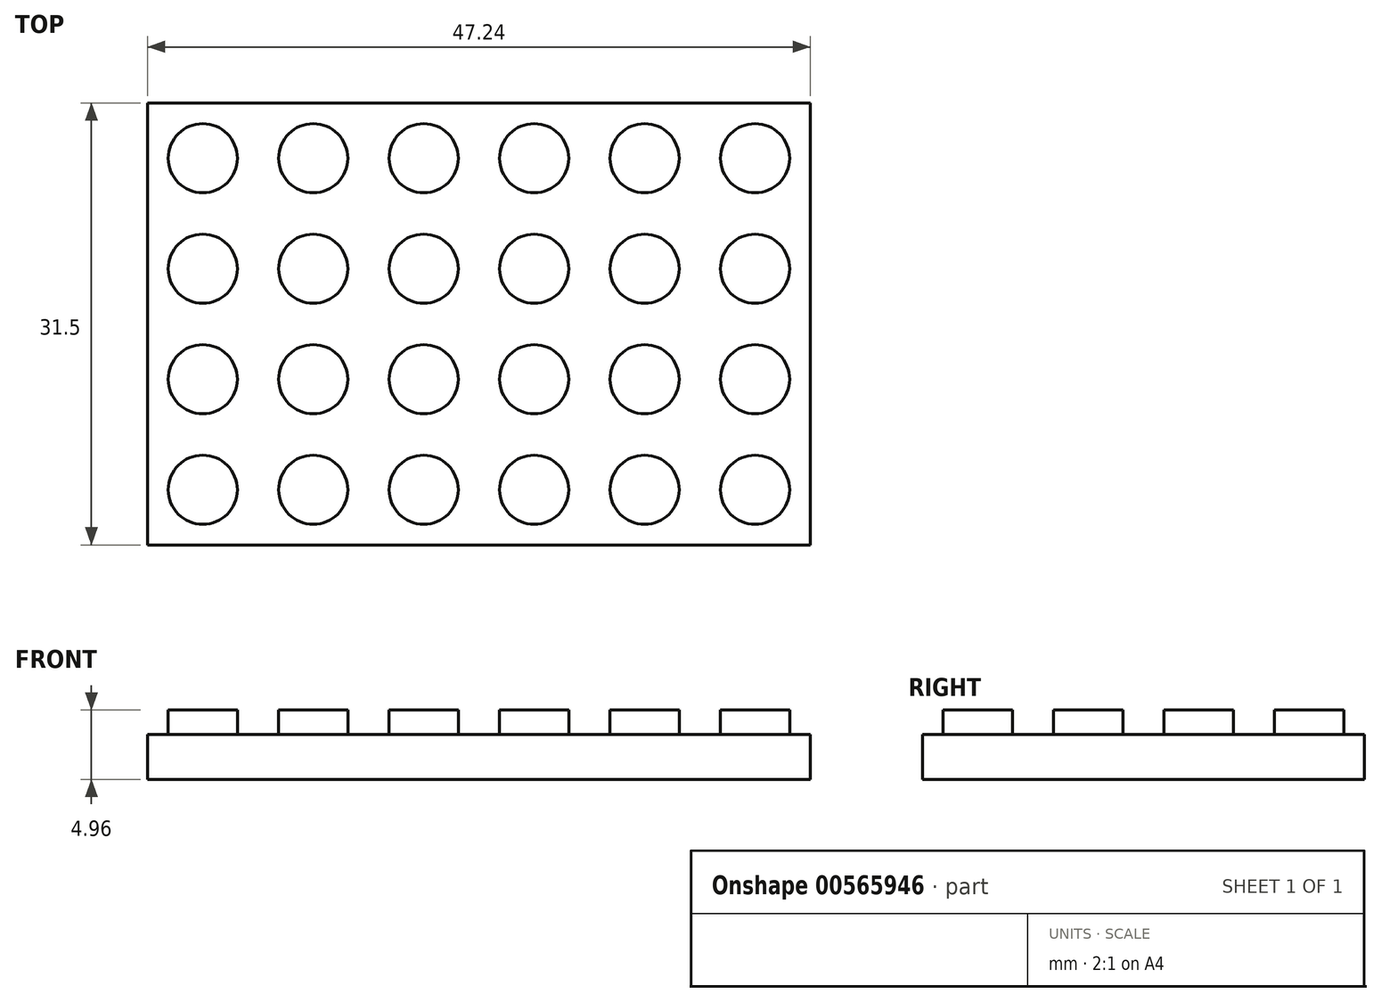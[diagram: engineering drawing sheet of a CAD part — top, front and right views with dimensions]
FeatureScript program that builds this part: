
annotation { "Feature Type Name" : "Feature", "Feature Type Description" : "" }
export const myFeature = defineFeature(function(context is Context, id is Id, definition is map)
    precondition{}
    {
        {
            var Q0;
            Q0=qCreatedBy(makeId("Top.planeOp"),FACE);
            var sketch = newSketch(context, id + "F0", { "sketchPlane" : qUnion([Q0])});
            skLineSegment(sketch, "E0.rect.bottom", {"start": v(23.62, 15.75) * mm, "end": v(-23.62, 15.75) * mm});
            skLineSegment(sketch, "E0.rect.top", {"start": v(23.62, -15.75) * mm, "end": v(-23.62, -15.75) * mm});
            skLineSegment(sketch, "E0.rect.left", {"start": v(23.62, 15.75) * mm, "end": v(23.62, -15.75) * mm});
            skLineSegment(sketch, "E0.rect.right", {"start": v(-23.62, 15.75) * mm, "end": v(-23.62, -15.75) * mm});
            skPoint(sketch, "E0.rect.middle", {"position": v(0, 0) * mm});
            skSolve(sketch);
        }
        {
            var Q0;
            Q0=makeQuery(id+"F0.imprint","IMPRINT",FACE,{"disambiguationData":[TD([[makeQuery(id+"F0.imprint","IMPRINT",EDGE,{"derivedFrom":sQuery(id+"F0.wireOp",EDGE,"E0.rect.bottom")}),1.0]])]});
            extrude(context, id + "F1", {"entities" : qUnion([Q0]), "depth" : 3.2 * mm});
        }
        {
            var Q0;
            Q0=makeQuery(id+"F1.opExtrude","CAP_FACE",FACE,{"disambiguationData":[OSD([sQuery(id+"F0.wireOp",EDGE,"E0.rect.bottom"),sQuery(id+"F0.wireOp",EDGE,"E0.rect.top"),sQuery(id+"F0.wireOp",EDGE,"E0.rect.left"),sQuery(id+"F0.wireOp",EDGE,"E0.rect.right")])],"isStart":false});
            var sketch = newSketch(context, id + "F2", { "sketchPlane" : qUnion([Q0])});
            skLineSegment(sketch, "E1", {"start": v(0, 0) * mm, "end": v(0, 7.87) * mm});
            skLineSegment(sketch, "E2", {"start": v(0, 7.87) * mm, "end": v(0, 15.75) * mm});
            skLineSegment(sketch, "E3", {"start": v(0, 0) * mm, "end": v(0, -7.87) * mm});
            skLineSegment(sketch, "E4", {"start": v(0, -7.87) * mm, "end": v(0, -15.75) * mm});
            skPoint(sketch, "E4.endSnap0", {"position": v(0, -15.75) * mm});
            skLineSegment(sketch, "E5", {"start": v(0, 0) * mm, "end": v(3.94, 0) * mm});
            skLineSegment(sketch, "E6", {"start": v(3.94, 0) * mm, "end": v(11.81, 0) * mm});
            skLineSegment(sketch, "E7", {"start": v(11.81, 0) * mm, "end": v(19.69, 0) * mm});
            skLineSegment(sketch, "E8", {"start": v(0, 0) * mm, "end": v(-3.94, 0) * mm});
            skLineSegment(sketch, "E9", {"start": v(-3.94, 0) * mm, "end": v(-11.81, 0) * mm});
            skLineSegment(sketch, "E10", {"start": v(-11.81, 0) * mm, "end": v(-19.69, 0) * mm});
            skLineSegment(sketch, "E11", {"start": v(-19.69, 0) * mm, "end": v(-19.69, -3.94) * mm});
            skLineSegment(sketch, "E12", {"start": v(-19.69, -3.94) * mm, "end": v(-19.69, -11.81) * mm});
            skLineSegment(sketch, "E13", {"start": v(-19.69, 0) * mm, "end": v(-19.69, 3.94) * mm});
            skLineSegment(sketch, "E14", {"start": v(-19.69, 3.94) * mm, "end": v(-19.69, 11.81) * mm});
            skLineSegment(sketch, "E15", {"start": v(-19.69, 3.94) * mm, "end": v(-11.81, 3.94) * mm});
            skLineSegment(sketch, "E16", {"start": v(-11.81, 3.94) * mm, "end": v(-3.94, 3.94) * mm});
            skLineSegment(sketch, "E17", {"start": v(-3.94, 3.94) * mm, "end": v(-3.94, 11.81) * mm});
            skLineSegment(sketch, "E18", {"start": v(-3.94, 11.81) * mm, "end": v(-11.81, 11.81) * mm});
            skLineSegment(sketch, "E19", {"start": v(-19.69, -3.94) * mm, "end": v(-11.81, -3.94) * mm});
            skLineSegment(sketch, "E20", {"start": v(-11.81, -3.94) * mm, "end": v(-3.94, -3.94) * mm});
            skLineSegment(sketch, "E21", {"start": v(-3.94, -3.94) * mm, "end": v(-3.94, -11.81) * mm});
            skLineSegment(sketch, "E22", {"start": v(-3.94, -11.81) * mm, "end": v(-11.81, -11.81) * mm});
            skLineSegment(sketch, "E23", {"start": v(3.94, 0) * mm, "end": v(3.94, 3.94) * mm});
            skPoint(sketch, "E23.endSnap0", {"position": v(0, 3.94) * mm});
            skLineSegment(sketch, "E24", {"start": v(3.94, 3.94) * mm, "end": v(3.94, 11.81) * mm});
            skPoint(sketch, "E24.endSnap0", {"position": v(0, 11.81) * mm});
            skLineSegment(sketch, "E25", {"start": v(3.94, 11.81) * mm, "end": v(11.81, 11.81) * mm});
            skLineSegment(sketch, "E26", {"start": v(11.81, 11.81) * mm, "end": v(19.69, 11.81) * mm});
            skLineSegment(sketch, "E27", {"start": v(19.69, 11.81) * mm, "end": v(19.69, 3.94) * mm});
            skLineSegment(sketch, "E28", {"start": v(19.69, 3.94) * mm, "end": v(11.81, 3.94) * mm});
            skLineSegment(sketch, "E29", {"start": v(3.94, 0) * mm, "end": v(3.94, -3.94) * mm});
            skPoint(sketch, "E29.endSnap0", {"position": v(0, -3.94) * mm});
            skLineSegment(sketch, "E30", {"start": v(3.94, -3.94) * mm, "end": v(3.94, -11.81) * mm});
            skPoint(sketch, "E30.endSnap0", {"position": v(0, -11.81) * mm});
            skLineSegment(sketch, "E31", {"start": v(3.94, -11.81) * mm, "end": v(11.81, -11.81) * mm});
            skLineSegment(sketch, "E32", {"start": v(11.81, -11.81) * mm, "end": v(19.69, -11.81) * mm});
            skLineSegment(sketch, "E33", {"start": v(19.69, -11.81) * mm, "end": v(19.69, -3.94) * mm});
            skLineSegment(sketch, "E34", {"start": v(19.69, -3.94) * mm, "end": v(11.81, -3.94) * mm});
            skCircle(sketch, "E35", {"center": v(-19.69, 11.81) * mm, "radius": 2.46 * mm});
            skCircle(sketch, "E36", {"center": v(-11.81, 11.81) * mm, "radius": 2.46 * mm});
            skCircle(sketch, "E37", {"center": v(-3.94, 11.81) * mm, "radius": 2.46 * mm});
            skCircle(sketch, "E38", {"center": v(3.94, 11.81) * mm, "radius": 2.46 * mm});
            skCircle(sketch, "E39", {"center": v(11.81, 11.81) * mm, "radius": 2.46 * mm});
            skCircle(sketch, "E40", {"center": v(19.69, 11.81) * mm, "radius": 2.46 * mm});
            skCircle(sketch, "E41", {"center": v(19.69, 3.94) * mm, "radius": 2.46 * mm});
            skCircle(sketch, "E42", {"center": v(11.81, 3.94) * mm, "radius": 2.46 * mm});
            skCircle(sketch, "E43", {"center": v(3.94, 3.94) * mm, "radius": 2.46 * mm});
            skCircle(sketch, "E44", {"center": v(-3.94, 3.94) * mm, "radius": 2.46 * mm});
            skCircle(sketch, "E45", {"center": v(-11.81, 3.94) * mm, "radius": 2.46 * mm});
            skCircle(sketch, "E46", {"center": v(-19.69, 3.94) * mm, "radius": 2.46 * mm});
            skCircle(sketch, "E47", {"center": v(-19.69, -3.94) * mm, "radius": 2.46 * mm});
            skCircle(sketch, "E48", {"center": v(-11.81, -3.94) * mm, "radius": 2.46 * mm});
            skCircle(sketch, "E49", {"center": v(-3.94, -3.94) * mm, "radius": 2.46 * mm});
            skCircle(sketch, "E50", {"center": v(-3.94, -11.81) * mm, "radius": 2.46 * mm});
            skCircle(sketch, "E51", {"center": v(-11.81, -11.81) * mm, "radius": 2.46 * mm});
            skCircle(sketch, "E52", {"center": v(-19.69, -11.81) * mm, "radius": 2.46 * mm});
            skCircle(sketch, "E53", {"center": v(3.94, -11.81) * mm, "radius": 2.46 * mm});
            skCircle(sketch, "E54", {"center": v(11.81, -11.81) * mm, "radius": 2.46 * mm});
            skCircle(sketch, "E55", {"center": v(19.69, -11.81) * mm, "radius": 2.46 * mm});
            skCircle(sketch, "E56", {"center": v(19.69, -3.94) * mm, "radius": 2.46 * mm});
            skCircle(sketch, "E57", {"center": v(11.81, -3.94) * mm, "radius": 2.46 * mm});
            skCircle(sketch, "E58", {"center": v(3.94, -3.94) * mm, "radius": 2.46 * mm});
            skSolve(sketch);
        }
        {
            var Q0;
            Q0=makeQuery(id+"F2.imprint","IMPRINT",FACE,{"disambiguationData":[TD([[makeQuery(id+"F2.imprint","IMPRINT",EDGE,{"derivedFrom":sQuery(id+"F2.wireOp",EDGE,"E35")}),1.0]])]});
            var Q1;
            Q1=makeQuery(id+"F2.imprint","IMPRINT",FACE,{"disambiguationData":[TD([[makeQuery(id+"F2.imprint","IMPRINT",EDGE,{"derivedFrom":sQuery(id+"F2.wireOp",EDGE,"E36")}),1.0]])]});
            var Q2;
            {var subQ0=sQuery(id+"F2.wireOp",EDGE,"E18");var subQ1=sQuery(id+"F2.wireOp",EDGE,"E17");var subQ2=makeQuery(id+"F2.imprint","INTERSECT",VERTEX,{"derivedFrom":[subQ1,subQ0]});Q2=makeQuery(id+"F2.imprint","IMPRINT",FACE,{"disambiguationData":[TD([[makeQuery(id+"F2.imprint","IMPRINT",EDGE,{"disambiguationData":[TD([[subQ2,1.0]])],"derivedFrom":subQ1}),-1.0]])]});}
            var Q3;
            {var subQ0=sQuery(id+"F2.wireOp",EDGE,"E18");var subQ1=sQuery(id+"F2.wireOp",EDGE,"E17");var subQ2=makeQuery(id+"F2.imprint","INTERSECT",VERTEX,{"derivedFrom":[subQ1,subQ0]});Q3=makeQuery(id+"F2.imprint","IMPRINT",FACE,{"disambiguationData":[TD([[makeQuery(id+"F2.imprint","IMPRINT",EDGE,{"disambiguationData":[TD([[subQ2,1.0]])],"derivedFrom":subQ1}),1.0]])]});}
            var Q4;
            {var subQ0=sQuery(id+"F2.wireOp",EDGE,"E25");var subQ1=sQuery(id+"F2.wireOp",EDGE,"E24");var subQ2=makeQuery(id+"F2.imprint","INTERSECT",VERTEX,{"derivedFrom":[subQ1,subQ0]});Q4=makeQuery(id+"F2.imprint","IMPRINT",FACE,{"disambiguationData":[TD([[makeQuery(id+"F2.imprint","IMPRINT",EDGE,{"disambiguationData":[TD([[subQ2,1.0]])],"derivedFrom":subQ1}),1.0]])]});}
            var Q5;
            {var subQ0=sQuery(id+"F2.wireOp",EDGE,"E25");var subQ1=sQuery(id+"F2.wireOp",EDGE,"E24");var subQ2=makeQuery(id+"F2.imprint","INTERSECT",VERTEX,{"derivedFrom":[subQ1,subQ0]});Q5=makeQuery(id+"F2.imprint","IMPRINT",FACE,{"disambiguationData":[TD([[makeQuery(id+"F2.imprint","IMPRINT",EDGE,{"disambiguationData":[TD([[subQ2,1.0]])],"derivedFrom":subQ1}),-1.0]])]});}
            var Q6;
            {var subQ0=sQuery(id+"F2.wireOp",EDGE,"E24");var subQ1=sQuery(id+"F2.wireOp",EDGE,"E23");var subQ2=makeQuery(id+"F2.imprint","INTERSECT",VERTEX,{"derivedFrom":[subQ1,subQ0]});Q6=makeQuery(id+"F2.imprint","IMPRINT",FACE,{"disambiguationData":[TD([[makeQuery(id+"F2.imprint","IMPRINT",EDGE,{"disambiguationData":[TD([[subQ2,1.0]])],"derivedFrom":subQ1}),-1.0]])]});}
            var Q7;
            {var subQ0=sQuery(id+"F2.wireOp",EDGE,"E24");var subQ1=sQuery(id+"F2.wireOp",EDGE,"E23");var subQ2=makeQuery(id+"F2.imprint","INTERSECT",VERTEX,{"derivedFrom":[subQ1,subQ0]});Q7=makeQuery(id+"F2.imprint","IMPRINT",FACE,{"disambiguationData":[TD([[makeQuery(id+"F2.imprint","IMPRINT",EDGE,{"disambiguationData":[TD([[subQ2,1.0]])],"derivedFrom":subQ1}),1.0]])]});}
            var Q8;
            {var subQ0=sQuery(id+"F2.wireOp",EDGE,"E17");var subQ1=sQuery(id+"F2.wireOp",EDGE,"E16");var subQ2=makeQuery(id+"F2.imprint","INTERSECT",VERTEX,{"derivedFrom":[subQ1,subQ0]});Q8=makeQuery(id+"F2.imprint","IMPRINT",FACE,{"disambiguationData":[TD([[makeQuery(id+"F2.imprint","IMPRINT",EDGE,{"disambiguationData":[TD([[subQ2,1.0]])],"derivedFrom":subQ1}),-1.0]])]});}
            var Q9;
            {var subQ0=sQuery(id+"F2.wireOp",EDGE,"E17");var subQ1=sQuery(id+"F2.wireOp",EDGE,"E16");var subQ2=makeQuery(id+"F2.imprint","INTERSECT",VERTEX,{"derivedFrom":[subQ1,subQ0]});Q9=makeQuery(id+"F2.imprint","IMPRINT",FACE,{"disambiguationData":[TD([[makeQuery(id+"F2.imprint","IMPRINT",EDGE,{"disambiguationData":[TD([[subQ2,1.0]])],"derivedFrom":subQ1}),1.0]])]});}
            var Q10;
            {var subQ0=sQuery(id+"F2.wireOp",EDGE,"E16");var subQ1=sQuery(id+"F2.wireOp",EDGE,"E15");var subQ2=makeQuery(id+"F2.imprint","INTERSECT",VERTEX,{"derivedFrom":[subQ1,subQ0]});Q10=makeQuery(id+"F2.imprint","IMPRINT",FACE,{"disambiguationData":[TD([[makeQuery(id+"F2.imprint","IMPRINT",EDGE,{"disambiguationData":[TD([[subQ2,1.0]])],"derivedFrom":subQ1}),1.0]])]});}
            var Q11;
            {var subQ0=sQuery(id+"F2.wireOp",EDGE,"E16");var subQ1=sQuery(id+"F2.wireOp",EDGE,"E15");var subQ2=makeQuery(id+"F2.imprint","INTERSECT",VERTEX,{"derivedFrom":[subQ1,subQ0]});Q11=makeQuery(id+"F2.imprint","IMPRINT",FACE,{"disambiguationData":[TD([[makeQuery(id+"F2.imprint","IMPRINT",EDGE,{"disambiguationData":[TD([[subQ2,1.0]])],"derivedFrom":subQ1}),-1.0]])]});}
            var Q12;
            {var subQ1=sQuery(id+"F2.wireOp",EDGE,"E14");var subQ3=sQuery(id+"F2.wireOp",EDGE,"E46");var subQ4=makeQuery(id+"F2.imprint","INTERSECT",VERTEX,{"derivedFrom":[subQ1,subQ3]});Q12=makeQuery(id+"F2.imprint","IMPRINT",FACE,{"disambiguationData":[TD([[makeQuery(id+"F2.imprint","IMPRINT",EDGE,{"disambiguationData":[TD([[subQ4,1.0]])],"derivedFrom":subQ3}),1.0]])]});}
            var Q13;
            {var subQ1=sQuery(id+"F2.wireOp",EDGE,"E13");var subQ3=sQuery(id+"F2.wireOp",EDGE,"E46");var subQ4=makeQuery(id+"F2.imprint","INTERSECT",VERTEX,{"derivedFrom":[subQ1,subQ3]});Q13=makeQuery(id+"F2.imprint","IMPRINT",FACE,{"disambiguationData":[TD([[makeQuery(id+"F2.imprint","IMPRINT",EDGE,{"disambiguationData":[TD([[subQ4,-1.0]])],"derivedFrom":subQ3}),1.0]])]});}
            var Q14;
            {var subQ1=sQuery(id+"F2.wireOp",EDGE,"E13");var subQ3=sQuery(id+"F2.wireOp",EDGE,"E46");var subQ4=makeQuery(id+"F2.imprint","INTERSECT",VERTEX,{"derivedFrom":[subQ1,subQ3]});Q14=makeQuery(id+"F2.imprint","IMPRINT",FACE,{"disambiguationData":[TD([[makeQuery(id+"F2.imprint","IMPRINT",EDGE,{"disambiguationData":[TD([[subQ4,1.0]])],"derivedFrom":subQ3}),1.0]])]});}
            var Q15;
            {var subQ1=sQuery(id+"F2.wireOp",EDGE,"E11");var subQ3=sQuery(id+"F2.wireOp",EDGE,"E47");var subQ4=makeQuery(id+"F2.imprint","INTERSECT",VERTEX,{"derivedFrom":[subQ1,subQ3]});Q15=makeQuery(id+"F2.imprint","IMPRINT",FACE,{"disambiguationData":[TD([[makeQuery(id+"F2.imprint","IMPRINT",EDGE,{"disambiguationData":[TD([[subQ4,1.0]])],"derivedFrom":subQ3}),1.0]])]});}
            var Q16;
            {var subQ1=sQuery(id+"F2.wireOp",EDGE,"E12");var subQ3=sQuery(id+"F2.wireOp",EDGE,"E47");var subQ4=makeQuery(id+"F2.imprint","INTERSECT",VERTEX,{"derivedFrom":[subQ1,subQ3]});Q16=makeQuery(id+"F2.imprint","IMPRINT",FACE,{"disambiguationData":[TD([[makeQuery(id+"F2.imprint","IMPRINT",EDGE,{"disambiguationData":[TD([[subQ4,-1.0]])],"derivedFrom":subQ3}),1.0]])]});}
            var Q17;
            {var subQ1=sQuery(id+"F2.wireOp",EDGE,"E11");var subQ3=sQuery(id+"F2.wireOp",EDGE,"E47");var subQ4=makeQuery(id+"F2.imprint","INTERSECT",VERTEX,{"derivedFrom":[subQ1,subQ3]});Q17=makeQuery(id+"F2.imprint","IMPRINT",FACE,{"disambiguationData":[TD([[makeQuery(id+"F2.imprint","IMPRINT",EDGE,{"disambiguationData":[TD([[subQ4,-1.0]])],"derivedFrom":subQ3}),1.0]])]});}
            var Q18;
            {var subQ0=sQuery(id+"F2.wireOp",EDGE,"E20");var subQ1=sQuery(id+"F2.wireOp",EDGE,"E19");var subQ2=makeQuery(id+"F2.imprint","INTERSECT",VERTEX,{"derivedFrom":[subQ1,subQ0]});Q18=makeQuery(id+"F2.imprint","IMPRINT",FACE,{"disambiguationData":[TD([[makeQuery(id+"F2.imprint","IMPRINT",EDGE,{"disambiguationData":[TD([[subQ2,1.0]])],"derivedFrom":subQ1}),1.0]])]});}
            var Q19;
            {var subQ0=sQuery(id+"F2.wireOp",EDGE,"E20");var subQ1=sQuery(id+"F2.wireOp",EDGE,"E19");var subQ2=makeQuery(id+"F2.imprint","INTERSECT",VERTEX,{"derivedFrom":[subQ1,subQ0]});Q19=makeQuery(id+"F2.imprint","IMPRINT",FACE,{"disambiguationData":[TD([[makeQuery(id+"F2.imprint","IMPRINT",EDGE,{"disambiguationData":[TD([[subQ2,1.0]])],"derivedFrom":subQ1}),-1.0]])]});}
            var Q20;
            {var subQ0=sQuery(id+"F2.wireOp",EDGE,"E21");var subQ1=sQuery(id+"F2.wireOp",EDGE,"E20");var subQ2=makeQuery(id+"F2.imprint","INTERSECT",VERTEX,{"derivedFrom":[subQ1,subQ0]});Q20=makeQuery(id+"F2.imprint","IMPRINT",FACE,{"disambiguationData":[TD([[makeQuery(id+"F2.imprint","IMPRINT",EDGE,{"disambiguationData":[TD([[subQ2,1.0]])],"derivedFrom":subQ1}),-1.0]])]});}
            var Q21;
            {var subQ0=sQuery(id+"F2.wireOp",EDGE,"E21");var subQ1=sQuery(id+"F2.wireOp",EDGE,"E20");var subQ2=makeQuery(id+"F2.imprint","INTERSECT",VERTEX,{"derivedFrom":[subQ1,subQ0]});Q21=makeQuery(id+"F2.imprint","IMPRINT",FACE,{"disambiguationData":[TD([[makeQuery(id+"F2.imprint","IMPRINT",EDGE,{"disambiguationData":[TD([[subQ2,1.0]])],"derivedFrom":subQ1}),1.0]])]});}
            var Q22;
            {var subQ0=sQuery(id+"F2.wireOp",EDGE,"E22");var subQ1=sQuery(id+"F2.wireOp",EDGE,"E21");var subQ2=makeQuery(id+"F2.imprint","INTERSECT",VERTEX,{"derivedFrom":[subQ1,subQ0]});Q22=makeQuery(id+"F2.imprint","IMPRINT",FACE,{"disambiguationData":[TD([[makeQuery(id+"F2.imprint","IMPRINT",EDGE,{"disambiguationData":[TD([[subQ2,1.0]])],"derivedFrom":subQ1}),1.0]])]});}
            var Q23;
            {var subQ0=sQuery(id+"F2.wireOp",EDGE,"E22");var subQ1=sQuery(id+"F2.wireOp",EDGE,"E21");var subQ2=makeQuery(id+"F2.imprint","INTERSECT",VERTEX,{"derivedFrom":[subQ1,subQ0]});Q23=makeQuery(id+"F2.imprint","IMPRINT",FACE,{"disambiguationData":[TD([[makeQuery(id+"F2.imprint","IMPRINT",EDGE,{"disambiguationData":[TD([[subQ2,1.0]])],"derivedFrom":subQ1}),-1.0]])]});}
            var Q24;
            Q24=makeQuery(id+"F2.imprint","IMPRINT",FACE,{"disambiguationData":[TD([[makeQuery(id+"F2.imprint","IMPRINT",EDGE,{"derivedFrom":sQuery(id+"F2.wireOp",EDGE,"E51")}),1.0]])]});
            var Q25;
            Q25=makeQuery(id+"F2.imprint","IMPRINT",FACE,{"disambiguationData":[TD([[makeQuery(id+"F2.imprint","IMPRINT",EDGE,{"derivedFrom":sQuery(id+"F2.wireOp",EDGE,"E52")}),1.0]])]});
            var Q26;
            {var subQ0=sQuery(id+"F2.wireOp",EDGE,"E31");var subQ1=sQuery(id+"F2.wireOp",EDGE,"E30");var subQ2=makeQuery(id+"F2.imprint","INTERSECT",VERTEX,{"derivedFrom":[subQ1,subQ0]});Q26=makeQuery(id+"F2.imprint","IMPRINT",FACE,{"disambiguationData":[TD([[makeQuery(id+"F2.imprint","IMPRINT",EDGE,{"disambiguationData":[TD([[subQ2,1.0]])],"derivedFrom":subQ1}),-1.0]])]});}
            var Q27;
            {var subQ0=sQuery(id+"F2.wireOp",EDGE,"E31");var subQ1=sQuery(id+"F2.wireOp",EDGE,"E30");var subQ2=makeQuery(id+"F2.imprint","INTERSECT",VERTEX,{"derivedFrom":[subQ1,subQ0]});Q27=makeQuery(id+"F2.imprint","IMPRINT",FACE,{"disambiguationData":[TD([[makeQuery(id+"F2.imprint","IMPRINT",EDGE,{"disambiguationData":[TD([[subQ2,1.0]])],"derivedFrom":subQ1}),1.0]])]});}
            var Q28;
            {var subQ0=sQuery(id+"F2.wireOp",EDGE,"E30");var subQ1=sQuery(id+"F2.wireOp",EDGE,"E29");var subQ2=makeQuery(id+"F2.imprint","INTERSECT",VERTEX,{"derivedFrom":[subQ1,subQ0]});Q28=makeQuery(id+"F2.imprint","IMPRINT",FACE,{"disambiguationData":[TD([[makeQuery(id+"F2.imprint","IMPRINT",EDGE,{"disambiguationData":[TD([[subQ2,1.0]])],"derivedFrom":subQ1}),1.0]])]});}
            var Q29;
            {var subQ0=sQuery(id+"F2.wireOp",EDGE,"E30");var subQ1=sQuery(id+"F2.wireOp",EDGE,"E29");var subQ2=makeQuery(id+"F2.imprint","INTERSECT",VERTEX,{"derivedFrom":[subQ1,subQ0]});Q29=makeQuery(id+"F2.imprint","IMPRINT",FACE,{"disambiguationData":[TD([[makeQuery(id+"F2.imprint","IMPRINT",EDGE,{"disambiguationData":[TD([[subQ2,1.0]])],"derivedFrom":subQ1}),-1.0]])]});}
            var Q30;
            Q30=makeQuery(id+"F2.imprint","IMPRINT",FACE,{"disambiguationData":[TD([[makeQuery(id+"F2.imprint","IMPRINT",EDGE,{"derivedFrom":sQuery(id+"F2.wireOp",EDGE,"E57")}),1.0]])]});
            var Q31;
            {var subQ0=sQuery(id+"F2.wireOp",EDGE,"E34");var subQ1=sQuery(id+"F2.wireOp",EDGE,"E33");var subQ2=makeQuery(id+"F2.imprint","INTERSECT",VERTEX,{"derivedFrom":[subQ1,subQ0]});Q31=makeQuery(id+"F2.imprint","IMPRINT",FACE,{"disambiguationData":[TD([[makeQuery(id+"F2.imprint","IMPRINT",EDGE,{"disambiguationData":[TD([[subQ2,1.0]])],"derivedFrom":subQ1}),-1.0]])]});}
            var Q32;
            {var subQ0=sQuery(id+"F2.wireOp",EDGE,"E34");var subQ1=sQuery(id+"F2.wireOp",EDGE,"E33");var subQ2=makeQuery(id+"F2.imprint","INTERSECT",VERTEX,{"derivedFrom":[subQ1,subQ0]});Q32=makeQuery(id+"F2.imprint","IMPRINT",FACE,{"disambiguationData":[TD([[makeQuery(id+"F2.imprint","IMPRINT",EDGE,{"disambiguationData":[TD([[subQ2,1.0]])],"derivedFrom":subQ1}),1.0]])]});}
            var Q33;
            {var subQ0=sQuery(id+"F2.wireOp",EDGE,"E33");var subQ1=sQuery(id+"F2.wireOp",EDGE,"E32");var subQ2=makeQuery(id+"F2.imprint","INTERSECT",VERTEX,{"derivedFrom":[subQ1,subQ0]});Q33=makeQuery(id+"F2.imprint","IMPRINT",FACE,{"disambiguationData":[TD([[makeQuery(id+"F2.imprint","IMPRINT",EDGE,{"disambiguationData":[TD([[subQ2,1.0]])],"derivedFrom":subQ1}),-1.0]])]});}
            var Q34;
            {var subQ0=sQuery(id+"F2.wireOp",EDGE,"E33");var subQ1=sQuery(id+"F2.wireOp",EDGE,"E32");var subQ2=makeQuery(id+"F2.imprint","INTERSECT",VERTEX,{"derivedFrom":[subQ1,subQ0]});Q34=makeQuery(id+"F2.imprint","IMPRINT",FACE,{"disambiguationData":[TD([[makeQuery(id+"F2.imprint","IMPRINT",EDGE,{"disambiguationData":[TD([[subQ2,1.0]])],"derivedFrom":subQ1}),1.0]])]});}
            var Q35;
            {var subQ0=sQuery(id+"F2.wireOp",EDGE,"E32");var subQ1=sQuery(id+"F2.wireOp",EDGE,"E31");var subQ2=makeQuery(id+"F2.imprint","INTERSECT",VERTEX,{"derivedFrom":[subQ1,subQ0]});Q35=makeQuery(id+"F2.imprint","IMPRINT",FACE,{"disambiguationData":[TD([[makeQuery(id+"F2.imprint","IMPRINT",EDGE,{"disambiguationData":[TD([[subQ2,1.0]])],"derivedFrom":subQ1}),1.0]])]});}
            var Q36;
            {var subQ0=sQuery(id+"F2.wireOp",EDGE,"E32");var subQ1=sQuery(id+"F2.wireOp",EDGE,"E31");var subQ2=makeQuery(id+"F2.imprint","INTERSECT",VERTEX,{"derivedFrom":[subQ1,subQ0]});Q36=makeQuery(id+"F2.imprint","IMPRINT",FACE,{"disambiguationData":[TD([[makeQuery(id+"F2.imprint","IMPRINT",EDGE,{"disambiguationData":[TD([[subQ2,1.0]])],"derivedFrom":subQ1}),-1.0]])]});}
            var Q37;
            {var subQ0=sQuery(id+"F2.wireOp",EDGE,"E28");var subQ1=sQuery(id+"F2.wireOp",EDGE,"E27");var subQ2=makeQuery(id+"F2.imprint","INTERSECT",VERTEX,{"derivedFrom":[subQ1,subQ0]});Q37=makeQuery(id+"F2.imprint","IMPRINT",FACE,{"disambiguationData":[TD([[makeQuery(id+"F2.imprint","IMPRINT",EDGE,{"disambiguationData":[TD([[subQ2,1.0]])],"derivedFrom":subQ1}),1.0]])]});}
            var Q38;
            {var subQ0=sQuery(id+"F2.wireOp",EDGE,"E28");var subQ1=sQuery(id+"F2.wireOp",EDGE,"E27");var subQ2=makeQuery(id+"F2.imprint","INTERSECT",VERTEX,{"derivedFrom":[subQ1,subQ0]});Q38=makeQuery(id+"F2.imprint","IMPRINT",FACE,{"disambiguationData":[TD([[makeQuery(id+"F2.imprint","IMPRINT",EDGE,{"disambiguationData":[TD([[subQ2,1.0]])],"derivedFrom":subQ1}),-1.0]])]});}
            var Q39;
            Q39=makeQuery(id+"F2.imprint","IMPRINT",FACE,{"disambiguationData":[TD([[makeQuery(id+"F2.imprint","IMPRINT",EDGE,{"derivedFrom":sQuery(id+"F2.wireOp",EDGE,"E42")}),1.0]])]});
            var Q40;
            {var subQ0=sQuery(id+"F2.wireOp",EDGE,"E26");var subQ1=sQuery(id+"F2.wireOp",EDGE,"E25");var subQ2=makeQuery(id+"F2.imprint","INTERSECT",VERTEX,{"derivedFrom":[subQ1,subQ0]});Q40=makeQuery(id+"F2.imprint","IMPRINT",FACE,{"disambiguationData":[TD([[makeQuery(id+"F2.imprint","IMPRINT",EDGE,{"disambiguationData":[TD([[subQ2,1.0]])],"derivedFrom":subQ1}),-1.0]])]});}
            var Q41;
            {var subQ0=sQuery(id+"F2.wireOp",EDGE,"E26");var subQ1=sQuery(id+"F2.wireOp",EDGE,"E25");var subQ2=makeQuery(id+"F2.imprint","INTERSECT",VERTEX,{"derivedFrom":[subQ1,subQ0]});Q41=makeQuery(id+"F2.imprint","IMPRINT",FACE,{"disambiguationData":[TD([[makeQuery(id+"F2.imprint","IMPRINT",EDGE,{"disambiguationData":[TD([[subQ2,1.0]])],"derivedFrom":subQ1}),1.0]])]});}
            var Q42;
            {var subQ0=sQuery(id+"F2.wireOp",EDGE,"E27");var subQ1=sQuery(id+"F2.wireOp",EDGE,"E26");var subQ2=makeQuery(id+"F2.imprint","INTERSECT",VERTEX,{"derivedFrom":[subQ1,subQ0]});Q42=makeQuery(id+"F2.imprint","IMPRINT",FACE,{"disambiguationData":[TD([[makeQuery(id+"F2.imprint","IMPRINT",EDGE,{"disambiguationData":[TD([[subQ2,1.0]])],"derivedFrom":subQ1}),1.0]])]});}
            var Q43;
            {var subQ0=sQuery(id+"F2.wireOp",EDGE,"E27");var subQ1=sQuery(id+"F2.wireOp",EDGE,"E26");var subQ2=makeQuery(id+"F2.imprint","INTERSECT",VERTEX,{"derivedFrom":[subQ1,subQ0]});Q43=makeQuery(id+"F2.imprint","IMPRINT",FACE,{"disambiguationData":[TD([[makeQuery(id+"F2.imprint","IMPRINT",EDGE,{"disambiguationData":[TD([[subQ2,1.0]])],"derivedFrom":subQ1}),-1.0]])]});}
            extrude(context, id + "F3", {"entities" : qUnion([Q0, Q1, Q2, Q3, Q4, Q5, Q6, Q7, Q8, Q9, Q10, Q11, Q12, Q13, Q14, Q15, Q16, Q17, Q18, Q19, Q20, Q21, Q22, Q23, Q24, Q25, Q26, Q27, Q28, Q29, Q30, Q31, Q32, Q33, Q34, Q35, Q36, Q37, Q38, Q39, Q40, Q41, Q42, Q43]), "operationType" : NewBodyOperationType.ADD, "depth" : 1.75 * mm});
        }
    });
